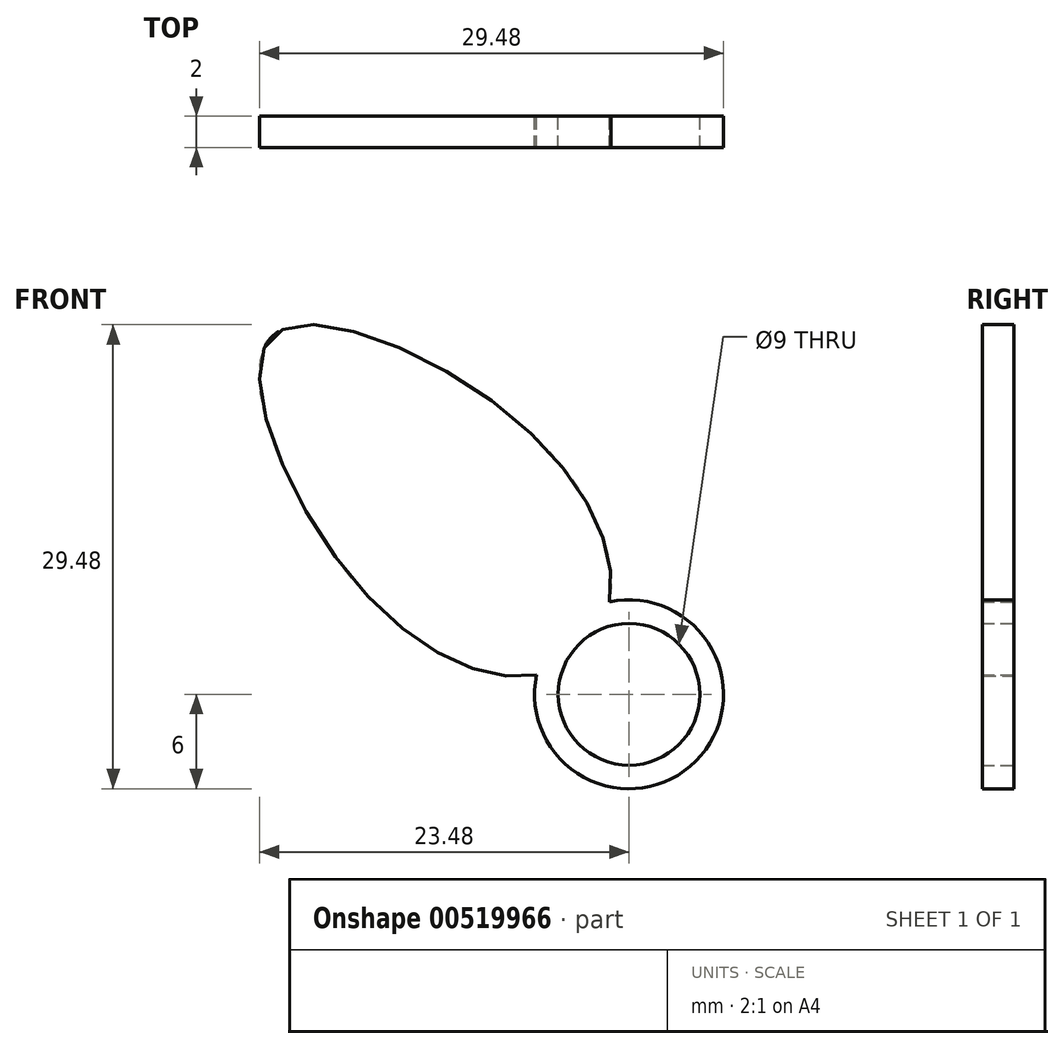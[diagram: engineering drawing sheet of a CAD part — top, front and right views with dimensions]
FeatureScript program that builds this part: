
annotation { "Feature Type Name" : "Feature", "Feature Type Description" : "" }
export const myFeature = defineFeature(function(context is Context, id is Id, definition is map)
    precondition{}
    {
        {
            var Q0;
            Q0=qCreatedBy(makeId("Front.planeOp"),FACE);
            var sketch = newSketch(context, id + "F0", { "sketchPlane" : qUnion([Q0])});
            skCircle(sketch, "E0", {"center": v(0, 0) * mm, "radius": 4.5 * mm});
            skCircle(sketch, "E1", {"center": v(0, 0) * mm, "radius": 6 * mm});
            skPoint(sketch, "E2.second.point", {"position": v(-17.5, 7.25) * mm});
            skPoint(sketch, "E2.third.point", {"position": v(-7.25, 17.5) * mm});
            skFitSpline(sketch, "E3", {"points": [v(-5.87, 1.24) * mm, v(-17.5, 7.25) * mm, v(-22.7, 22.7) * mm, v(-7.25, 17.5) * mm, v(-1.25, 5.87) * mm, v(-5.87, 1.24) * mm]});
            skSolve(sketch);
        }
        {
            var Q0;
            Q0 = qSketchRegion(id + "F0", true);
            extrude(context, id + "F1", {"entities" : qUnion([Q0]), "depth" : 2 * mm, "offsetDistance" : 25 * mm});
        }
    });
